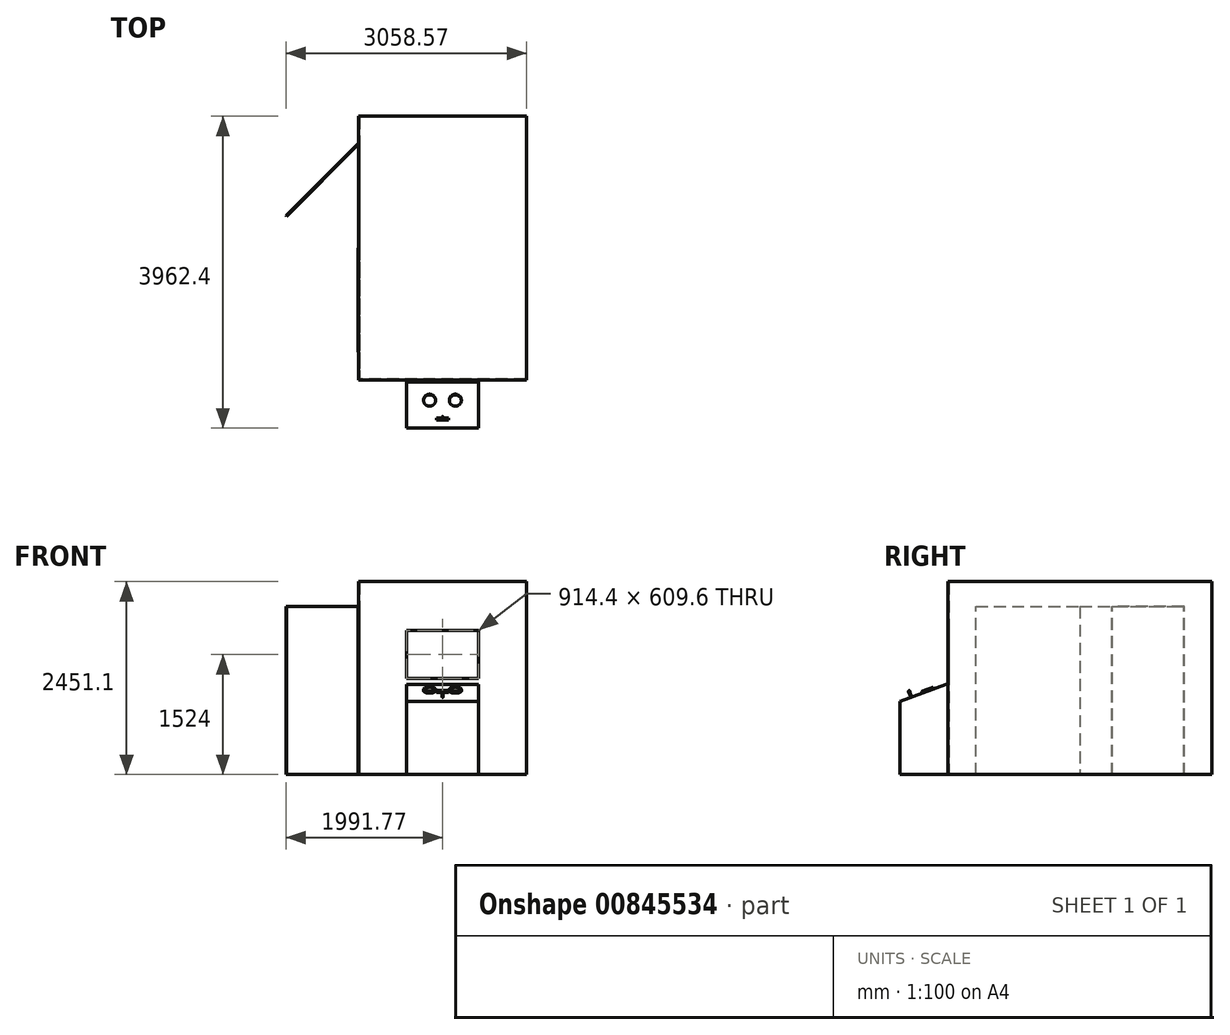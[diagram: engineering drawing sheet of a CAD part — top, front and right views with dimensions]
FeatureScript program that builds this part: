
annotation { "Feature Type Name" : "Feature", "Feature Type Description" : "" }
export const myFeature = defineFeature(function(context is Context, id is Id, definition is map)
    precondition{}
    {
        {
            var Q0;
            Q0=qCreatedBy(makeId("Top.planeOp"),FACE);
            var sketch = newSketch(context, id + "F0", { "sketchPlane" : qUnion([Q0])});
            skLineSegment(sketch, "E0.bottom", {"start": v(-1066.8, 1676.4) * mm, "end": v(1066.8, 1676.4) * mm});
            skLineSegment(sketch, "E0.top", {"start": v(-1066.8, -1676.4) * mm, "end": v(1066.8, -1676.4) * mm});
            skLineSegment(sketch, "E0.left", {"start": v(-1066.8, 1676.4) * mm, "end": v(-1066.8, -1676.4) * mm});
            skLineSegment(sketch, "E0.right", {"start": v(1066.8, 1676.4) * mm, "end": v(1066.8, -1676.4) * mm});
            skPoint(sketch, "E0.middle", {"position": v(0, 0) * mm});
            skLineSegment(sketch, "E1.bottom", {"start": v(1054.1, 1663.7) * mm, "end": v(-1054.1, 1663.7) * mm});
            skLineSegment(sketch, "E1.top", {"start": v(1054.1, -1663.7) * mm, "end": v(-1054.1, -1663.7) * mm});
            skLineSegment(sketch, "E1.left", {"start": v(1054.1, 1663.7) * mm, "end": v(1054.1, -1663.7) * mm});
            skLineSegment(sketch, "E1.right", {"start": v(-1054.1, 1663.7) * mm, "end": v(-1054.1, -1663.7) * mm});
            skSolve(sketch);
        }
        {
            var Q0;
            Q0 = qSketchRegion(id + "F0", true);
            extrude(context, id + "F1", {"entities" : qUnion([Q0]), "depth" : 2438.4 * mm, "offsetDistance" : 25.4 * mm});
        }
        {
            var Q0;
            Q0=makeQuery(id+"F1.opExtrude","SWEPT_FACE",FACE,{"disambiguationData":[OSD([sQuery(id+"F0.wireOp",EDGE,"E0.left")])]});
            var sketch = newSketch(context, id + "F2", { "sketchPlane" : qUnion([Q0])});
            skLineSegment(sketch, "E2.bottom", {"start": v(1320.8, 0) * mm, "end": v(0, 0) * mm});
            skLineSegment(sketch, "E2.top", {"start": v(1320.8, 2133.6) * mm, "end": v(0, 2133.6) * mm});
            skLineSegment(sketch, "E2.left", {"start": v(1320.8, 0) * mm, "end": v(1320.8, 2133.6) * mm});
            skLineSegment(sketch, "E2.right", {"start": v(0, 0) * mm, "end": v(0, 2133.6) * mm});
            skSolve(sketch);
        }
        {
            var Q0;
            Q0 = qSketchRegion(id + "F2", true);
            extrude(context, id + "F3", {"entities" : qUnion([Q0]), "operationType" : NewBodyOperationType.ADD, "depth" : 6.35 * mm, "offsetDistance" : 25.4 * mm});
        }
        {
            var Q0;
            Q0=makeQuery(id+"F1.opExtrude","SWEPT_FACE",FACE,{"disambiguationData":[OSD([sQuery(id+"F0.wireOp",EDGE,"E0.left")])]});
            var sketch = newSketch(context, id + "F4", { "sketchPlane" : qUnion([Q0])});
            skLineSegment(sketch, "E3.bottom", {"start": v(0, 0) * mm, "end": v(-1320.8, 0) * mm});
            skLineSegment(sketch, "E3.top", {"start": v(0, 2133.6) * mm, "end": v(-1320.8, 2133.6) * mm});
            skLineSegment(sketch, "E3.left", {"start": v(0, 0) * mm, "end": v(0, 2133.6) * mm});
            skLineSegment(sketch, "E3.right", {"start": v(-1320.8, 0) * mm, "end": v(-1320.8, 2133.6) * mm});
            skSolve(sketch);
        }
        {
            var Q0;
            Q0=makeQuery(id+"F4.imprint","IMPRINT",FACE,{"disambiguationData":[TD([[makeQuery(id+"F4.imprint","IMPRINT",EDGE,{"derivedFrom":sQuery(id+"F4.wireOp",EDGE,"E3.bottom")}),1.0]])]});
            extrude(context, id + "F5", {"entities" : qUnion([Q0]), "operationType" : NewBodyOperationType.REMOVE, "oppositeDirection" : true, "depth" : 25.4 * mm, "offsetDistance" : 25.4 * mm});
        }
        {
            var Q0;
            Q0=makeQuery(id+"F5.boolean.opBoolean","COPY",FACE,{"derivedFrom":makeQuery(id+"F5.opExtrude","SWEPT_FACE",FACE,{"disambiguationData":[OSD([sQuery(id+"F4.wireOp",EDGE,"E3.top")])]})});
            var sketch = newSketch(context, id + "F6", { "sketchPlane" : qUnion([Q0])});
            skLineSegment(sketch, "E4", {"start": v(-1066.8, -1320.8) * mm, "end": v(-1982.79, -404.81) * mm});
            skLineSegment(sketch, "E5", {"start": v(-1982.79, -404.81) * mm, "end": v(-1991.77, -413.8) * mm});
            skLineSegment(sketch, "E6", {"start": v(-1991.77, -413.8) * mm, "end": v(-1075.78, -1329.78) * mm});
            skLineSegment(sketch, "E7", {"start": v(-1075.78, -1329.78) * mm, "end": v(-1066.8, -1320.8) * mm});
            skSolve(sketch);
        }
        {
            var Q0;
            Q0 = qSketchRegion(id + "F6", true);
            extrude(context, id + "F7", {"entities" : qUnion([Q0]), "depth" : 2133.6 * mm, "offsetDistance" : 25.4 * mm});
        }
        {
            var Q0;
            Q0=makeQuery(id+"F1.opExtrude","SWEPT_FACE",FACE,{"disambiguationData":[OSD([sQuery(id+"F0.wireOp",EDGE,"E0.top")])]});
            var sketch = newSketch(context, id + "F8", { "sketchPlane" : qUnion([Q0])});
            skLineSegment(sketch, "E8.bottom", {"start": v(-457.2, 1828.8) * mm, "end": v(457.2, 1828.8) * mm});
            skLineSegment(sketch, "E8.top", {"start": v(-457.2, 1219.2) * mm, "end": v(457.2, 1219.2) * mm});
            skLineSegment(sketch, "E8.left", {"start": v(-457.2, 1828.8) * mm, "end": v(-457.2, 1219.2) * mm});
            skLineSegment(sketch, "E8.right", {"start": v(457.2, 1828.8) * mm, "end": v(457.2, 1219.2) * mm});
            skSolve(sketch);
        }
        {
            var Q0;
            Q0 = qSketchRegion(id + "F8", true);
            extrude(context, id + "F9", {"entities" : qUnion([Q0]), "operationType" : NewBodyOperationType.REMOVE, "oppositeDirection" : true, "depth" : 25.4 * mm, "offsetDistance" : 25.4 * mm});
        }
        {
            var Q0;
            Q0=makeQuery(id+"F1.opExtrude","SWEPT_FACE",FACE,{"disambiguationData":[OSD([sQuery(id+"F0.wireOp",EDGE,"E0.top")])]});
            var sketch = newSketch(context, id + "F10", { "sketchPlane" : qUnion([Q0])});
            skLineSegment(sketch, "E9.bottom", {"start": v(-457.2, 0) * mm, "end": v(457.2, 0) * mm});
            skLineSegment(sketch, "E9.top", {"start": v(-457.2, 1143) * mm, "end": v(457.2, 1143) * mm});
            skLineSegment(sketch, "E9.left", {"start": v(-457.2, 0) * mm, "end": v(-457.2, 1143) * mm});
            skLineSegment(sketch, "E9.right", {"start": v(457.2, 0) * mm, "end": v(457.2, 1143) * mm});
            skSolve(sketch);
        }
        {
            var Q0;
            Q0 = qSketchRegion(id + "F10", true);
            extrude(context, id + "F11", {"entities" : qUnion([Q0]), "operationType" : NewBodyOperationType.ADD, "depth" : 609.6 * mm, "offsetDistance" : 25.4 * mm});
        }
        {
            var Q0;
            Q0=makeQuery(id+"F11.opExtrude","SWEPT_FACE",FACE,{"disambiguationData":[OSD([sQuery(id+"F10.wireOp",EDGE,"E9.left")])]});
            var sketch = newSketch(context, id + "F12", { "sketchPlane" : qUnion([Q0])});
            skLineSegment(sketch, "E10", {"start": v(1701.8, 1143) * mm, "end": v(2286, 930.37) * mm});
            skLineSegment(sketch, "E11", {"start": v(2286, 930.37) * mm, "end": v(2286, 1143) * mm});
            skLineSegment(sketch, "E12", {"start": v(2286, 1143) * mm, "end": v(1701.8, 1143) * mm});
            skSolve(sketch);
        }
        {
            var Q0;
            Q0 = qSketchRegion(id + "F12", true);
            extrude(context, id + "F13", {"entities" : qUnion([Q0]), "operationType" : NewBodyOperationType.REMOVE, "endBound" : BoundingType.THROUGH_ALL, "oppositeDirection" : true, "depth" : 25.4 * mm, "offsetDistance" : 25.4 * mm});
        }
        {
            var Q0;
            Q0=makeQuery(id+"F13.boolean.opBoolean","COPY",FACE,{"derivedFrom":makeQuery(id+"F13.opExtrude","SWEPT_FACE",FACE,{"disambiguationData":[OSD([sQuery(id+"F12.wireOp",EDGE,"E10")])]})});
            var sketch = newSketch(context, id + "F14", { "sketchPlane" : qUnion([Q0])});
            skCircle(sketch, "E13", {"center": v(160.37, -1447.1) * mm, "radius": 76.2 * mm});
            skCircle(sketch, "E14", {"center": v(-166.63, -1447.1) * mm, "radius": 76.2 * mm});
            skSolve(sketch);
        }
        {
            var Q0;
            Q0 = qSketchRegion(id + "F14", true);
            extrude(context, id + "F15", {"entities" : qUnion([Q0]), "operationType" : NewBodyOperationType.ADD, "depth" : 25.4 * mm, "offsetDistance" : 25.4 * mm});
        }
        {
            var Q0;
            Q0=makeQuery(id+"F13.boolean.opBoolean","COPY",FACE,{"derivedFrom":makeQuery(id+"F13.opExtrude","SWEPT_FACE",FACE,{"disambiguationData":[OSD([sQuery(id+"F12.wireOp",EDGE,"E10")])]})});
            var sketch = newSketch(context, id + "F16", { "sketchPlane" : qUnion([Q0])});
            skCircle(sketch, "E15", {"center": v(0, -1677.53) * mm, "radius": 6.35 * mm});
            skSolve(sketch);
        }
        {
            var Q0;
            Q0 = qSketchRegion(id + "F16", true);
            extrude(context, id + "F17", {"entities" : qUnion([Q0]), "operationType" : NewBodyOperationType.ADD, "depth" : 76.2 * mm, "offsetDistance" : 25.4 * mm});
        }
        {
            var Q0;
            Q0=makeQuery(id+"F17.opExtrude","CAP_FACE",FACE,{"disambiguationData":[OSD([sQuery(id+"F16.wireOp",EDGE,"E15")])],"isStart":false});
            var sketch = newSketch(context, id + "F18", { "sketchPlane" : qUnion([Q0])});
            skLineSegment(sketch, "E16", {"start": v(76.2, -1664.83) * mm, "end": v(-76.2, -1664.83) * mm});
            skLineSegment(sketch, "E17", {"start": v(-76.2, -1664.83) * mm, "end": v(-76.2, -1677.53) * mm});
            skLineSegment(sketch, "E18", {"start": v(-76.2, -1677.53) * mm, "end": v(76.2, -1677.53) * mm});
            skLineSegment(sketch, "E19", {"start": v(76.2, -1677.53) * mm, "end": v(76.2, -1664.83) * mm});
            skPoint(sketch, "E20", {"position": v(0, -1677.53) * mm});
            skSolve(sketch);
        }
        {
            var Q0;
            Q0 = qSketchRegion(id + "F18", true);
            var Q1;
            Q1=sQuery(id+"F18.wireOp",EDGE,"E18");
            revolve(context, id + "F19", {"operationType" : NewBodyOperationType.ADD, "surfaceOperationType" : NewSurfaceOperationType.NEW, "entities" : qUnion([Q0]), "axis" : qUnion([Q1]), "revolveType" : RevolveType.FULL});
        }
        {
            var Q0;
            Q0=makeQuery(id+"F1.opExtrude","CAP_FACE",FACE,{"disambiguationData":[OSD([sQuery(id+"F0.wireOp",EDGE,"E0.bottom"),sQuery(id+"F0.wireOp",EDGE,"E0.top"),sQuery(id+"F0.wireOp",EDGE,"E0.left"),sQuery(id+"F0.wireOp",EDGE,"E0.right"),sQuery(id+"F0.wireOp",EDGE,"E1.bottom"),sQuery(id+"F0.wireOp",EDGE,"E1.top"),sQuery(id+"F0.wireOp",EDGE,"E1.left"),sQuery(id+"F0.wireOp",EDGE,"E1.right")])],"isStart":false});
            var sketch = newSketch(context, id + "F20", { "sketchPlane" : qUnion([Q0])});
            skLineSegment(sketch, "E21.0", {"start": v(-1066.8, 1676.4) * mm, "end": v(1066.8, 1676.4) * mm});
            skLineSegment(sketch, "E22.0", {"start": v(-1066.8, 1676.4) * mm, "end": v(-1066.8, -1676.4) * mm});
            skLineSegment(sketch, "E22.1", {"start": v(1066.8, 1676.4) * mm, "end": v(1066.8, -1676.4) * mm});
            skLineSegment(sketch, "E22.2", {"start": v(-1066.8, -1676.4) * mm, "end": v(1066.8, -1676.4) * mm});
            skSolve(sketch);
        }
        {
            var Q0;
            Q0 = qSketchRegion(id + "F20", true);
            extrude(context, id + "F21", {"entities" : qUnion([Q0]), "operationType" : NewBodyOperationType.ADD, "depth" : 12.7 * mm, "offsetDistance" : 25.4 * mm});
        }
    });
